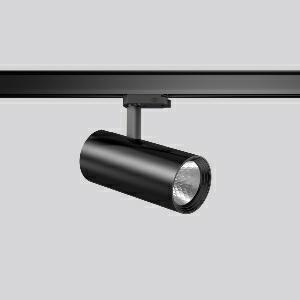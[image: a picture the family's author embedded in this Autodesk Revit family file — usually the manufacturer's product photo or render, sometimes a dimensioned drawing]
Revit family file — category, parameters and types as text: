
# Revit family: deecos_s_mini_742205_003_3_76_a47d
name_source: partatom
category: Lighting Fixtures
units: mm (PartAtom-declared; Revit-internal decimal feet)

## family parameters
Cut with Voids When Loaded = No
Host = Face
Light Source = No
Part Type = Normal
Room Calculation Point = No
Round Connector Dimension = Use Diameter
Shared = No

## types (1)
- DEECOS S mini (1 x LED Modul 935, 3800 lm, 3500)
    Apparent Load = 29 VA
    Approval mark = CE
    CIE Flux Codes = 95 99 100 100 100
    Color Rendering = 92
    Color Temperature = 3500
    Default Elevation = 1800 mm
    Description = Series: DEECOS S mini
LED surface-mounted projector in modern design with no visible cooling ribs. Housing: die-cast aluminium, powder-coated. Rotation range: 356°. Swivel range: 90°. Black plastic ring and recessed LED to prevent glare from the side. Optical assembly with reflector made of MIRO-Silver with 98% total light reflection for outstanding efficiency - can be changed without tools. Best colour rendering index Ra>90. With adapter for RZB 3-circuit DALI tracks. Suitable for Track on ceiling, Wall track. High quality converter without flickering and stroboscopic effect. The following accessories can be mounted without use of tools: interchangeable lenses, decorative glasses, honeycomb louvre, clear and frosted diffusers, white interchangeable plastic ring. 
Colour: deep black, matt (RAL 9005)
Diameter: 87 mm
Height: 214 mm
Lamp: LED
Socket: without socket
Colour temperature: 3500K
Colour rendering index (CRI): 92
System power: 29 W
Rated luminous flux: 3800 lm
Luminous efficiency: 131 lm/W
Control gear: Converter, dimmable, DALI
Protection class: I
Type of protection: IP 20
    Height = 214 mm
    Lamp = 1 x LED Modul 935
    Lamp Light Flux = 3800 lm
    Lamp count = 1
    Length = 87 mm
    Lifetime = 50000 h
    Luminous efficacy = 131 lm/W
    Manufacturer = RZB
    ModVariant = No
    Model = 742205.003.3.76
    Mounting Place = Ceiling
    Mounting Type = Rail mounted
    Number of Poles = 1
    OnlyDefault = Yes
    Power Factor = 1
    Product Name = DEECOS S mini
    Product group = Track mounted projectors
    ProductGroupID = 301
    Protection Class = Protection class I
    Protection Degree = IP 20
    RLX_Detail_Level = 1
    RLX_Emergency_Light_Flux = 0 lm
    RLX_Emergency_Type = 0
    RLX_Emergency_Type_DB = No
    RlxData = <blob elided: 39121 chars, md5=e2f78acc>
    Socket = socket
    Standby Power = 0 W
    System Light Flux = 3800 lm
    System Power = 29 W
    Type Comments = Product without accessories
    Type Image = 741926.003.jpg
    URL = http://relux.com
    VarID = ---
    Voltage = 230 V
    Voltage Range = 220-240 V
    Weight = 0.00 kg
    Width = 0 mm  [stored 0 ft]

note: [stored X ft] marks values corroborated as IEEE doubles in the binary element streams (Revit-internal decimal feet)

## geometry (parser evidence)
native form markers: Blend x4, Sweep x12
no freeform markers — native parametric forms only
